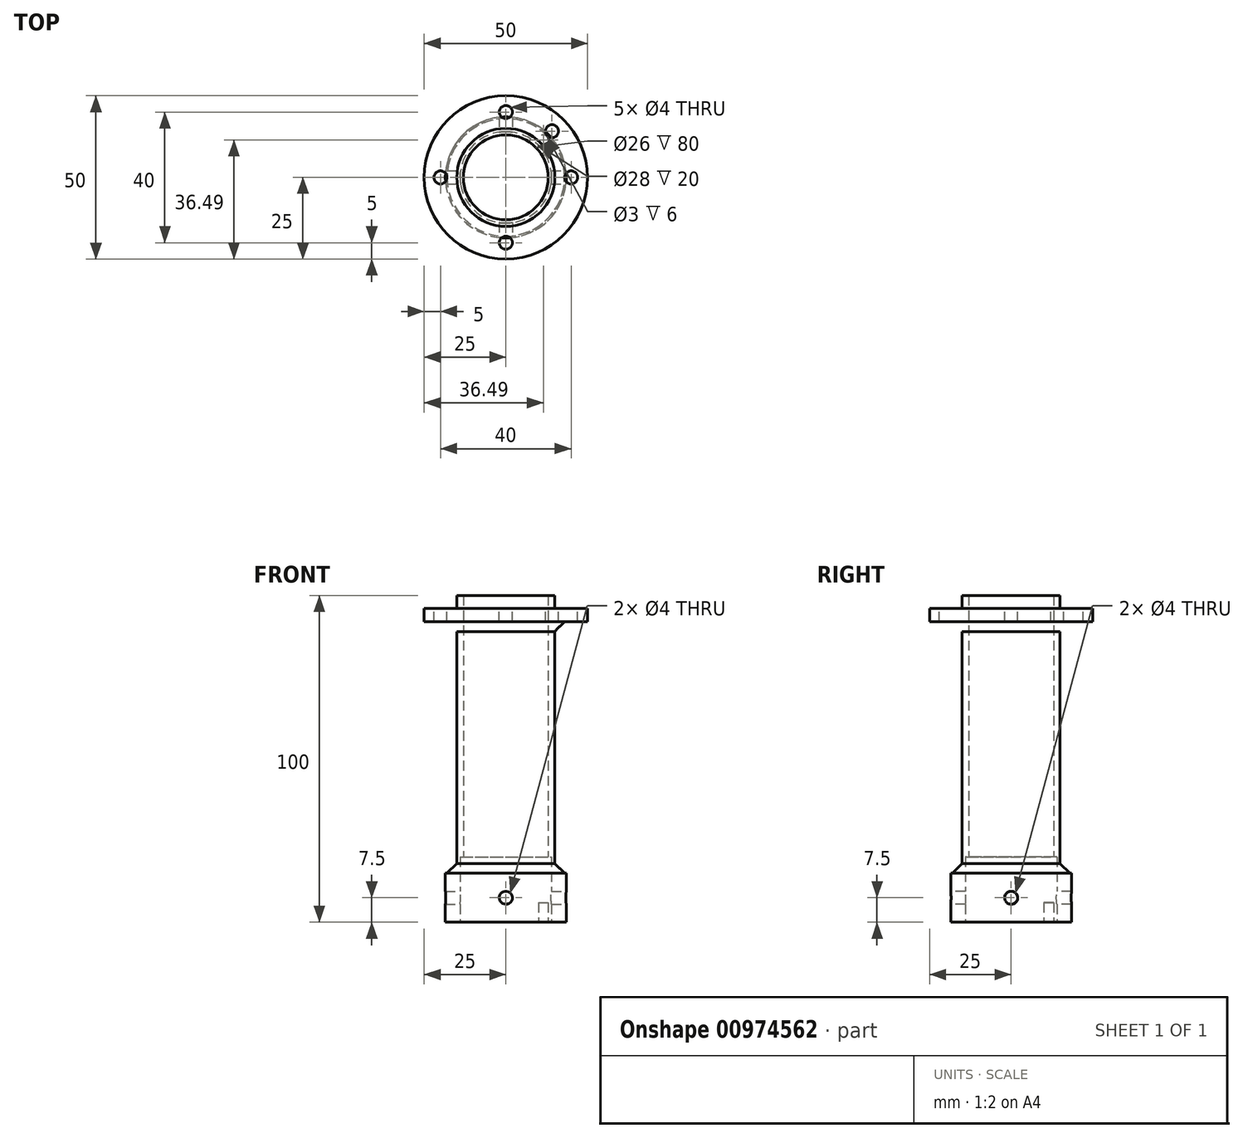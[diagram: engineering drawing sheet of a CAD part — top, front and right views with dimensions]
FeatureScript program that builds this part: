
annotation { "Feature Type Name" : "Feature", "Feature Type Description" : "" }
export const myFeature = defineFeature(function(context is Context, id is Id, definition is map)
    precondition{}
    {
        {
            var Q0;
            Q0=qCreatedBy(makeId("Top.planeOp"),FACE);
            var sketch = newSketch(context, id + "F0", { "sketchPlane" : qUnion([Q0])});
            skCircle(sketch, "E0", {"center": v(0, 0) * mm, "radius": 13 * mm});
            skCircle(sketch, "E1", {"center": v(0, 0) * mm, "radius": 15 * mm});
            skSolve(sketch);
        }
        {
            var Q0;
            Q0 = qSketchRegion(id + "F0", true);
            extrude(context, id + "F1", {"entities" : qUnion([Q0]), "depth" : 100 * mm, "offsetDistance" : 25 * mm});
        }
        {
            var Q0;
            Q0=makeQuery(id+"F1.opExtrude","CAP_FACE",FACE,{"disambiguationData":[OSD([sQuery(id+"F0.wireOp",EDGE,"E0"),sQuery(id+"F0.wireOp",EDGE,"E1")])],"isStart":false});
            cPlane(context, id + "F2", {"entities" : qUnion([Q0]), "cplaneType" : CPlaneType.OFFSET, "offset" : 4 * mm, "oppositeDirection" : true, "width" : 150 * mm, "height" : 150 * mm});
        }
        {
            var Q0;
            Q0=qCreatedBy(id+"F2.planeOp",FACE);
            var sketch = newSketch(context, id + "F3", { "sketchPlane" : qUnion([Q0])});
            skCircle(sketch, "E2", {"center": v(0, 0) * mm, "radius": 25 * mm});
            skCircle(sketch, "E3.0", {"center": v(0, 0) * mm, "radius": 15 * mm});
            skSolve(sketch);
        }
        {
            var Q0;
            Q0 = qSketchRegion(id + "F3", true);
            extrude(context, id + "F4", {"entities" : qUnion([Q0]), "operationType" : NewBodyOperationType.ADD, "oppositeDirection" : true, "depth" : 4 * mm, "offsetDistance" : 25 * mm});
        }
        {
            var Q0;
            Q0=makeQuery(id+"F4.opExtrude","CAP_FACE",FACE,{"disambiguationData":[OSD([sQuery(id+"F3.wireOp",EDGE,"E2"),sQuery(id+"F3.wireOp",EDGE,"E3.0")])],"isStart":true});
            var sketch = newSketch(context, id + "F5", { "sketchPlane" : qUnion([Q0])});
            skCircle(sketch, "E4", {"center": v(0, 20) * mm, "radius": 2 * mm});
            skCircle(sketch, "E5.1.0", {"center": v(-20, 0) * mm, "radius": 2 * mm});
            skCircle(sketch, "E5.2.0", {"center": v(0, -20) * mm, "radius": 2 * mm});
            skCircle(sketch, "E5.3.0", {"center": v(20, 0) * mm, "radius": 2 * mm});
            skPoint(sketch, "E5.center", {"position": v(0, 0) * mm});
            skSolve(sketch);
        }
        {
            var Q0;
            Q0 = qSketchRegion(id + "F5", true);
            extrude(context, id + "F6", {"entities" : qUnion([Q0]), "operationType" : NewBodyOperationType.REMOVE, "endBound" : BoundingType.THROUGH_ALL, "oppositeDirection" : true, "depth" : 25 * mm, "offsetDistance" : 25 * mm});
        }
        {
            var Q0;
            Q0=qCreatedBy(makeId("Top.planeOp"),FACE);
            var sketch = newSketch(context, id + "F7", { "sketchPlane" : qUnion([Q0])});
            skCircle(sketch, "E6", {"center": v(0, 0) * mm, "radius": 18.5 * mm});
            skCircle(sketch, "E7.0", {"center": v(0, 0) * mm, "radius": 13 * mm});
            skSolve(sketch);
        }
        {
            var Q0;
            Q0 = qSketchRegion(id + "F7", true);
            extrude(context, id + "F8", {"entities" : qUnion([Q0]), "operationType" : NewBodyOperationType.ADD, "depth" : 15 * mm, "offsetDistance" : 25 * mm});
        }
        {
            var Q0;
            Q0=qCreatedBy(makeId("Right.planeOp"),FACE);
            var sketch = newSketch(context, id + "F9", { "sketchPlane" : qUnion([Q0])});
            skLineSegment(sketch, "E8", {"start": v(-13, 0) * mm, "end": v(-13, 150) * mm, "construction": true});
            skLineSegment(sketch, "E9", {"start": v(13, 150) * mm, "end": v(13, 0) * mm, "construction": true});
            skLineSegment(sketch, "E10", {"start": v(-18.5, 0) * mm, "end": v(-18.5, 15) * mm, "construction": true});
            skLineSegment(sketch, "E11", {"start": v(18.5, 15) * mm, "end": v(18.5, 0) * mm, "construction": true});
            skLineSegment(sketch, "E12", {"start": v(15.75, 21.45) * mm, "end": v(15.75, -7.93) * mm, "construction": true});
            skLineSegment(sketch, "E13", {"start": v(24.83, 7.5) * mm, "end": v(-29.09, 7.5) * mm, "construction": true});
            skLineSegment(sketch, "E14", {"start": v(-15.75, 20.66) * mm, "end": v(-15.75, -8.82) * mm, "construction": true});
            skCircle(sketch, "E15", {"center": v(0, 7.5) * mm, "radius": 2 * mm});
            skSolve(sketch);
        }
        {
            var Q0;
            Q0 = qSketchRegion(id + "F9", true);
            extrude(context, id + "F10", {"entities" : qUnion([Q0]), "operationType" : NewBodyOperationType.REMOVE, "endBound" : BoundingType.SYMMETRIC, "oppositeDirection" : true, "depth" : 100 * mm, "offsetDistance" : 25 * mm});
        }
        {
            var Q0;
            Q0=qCreatedBy(makeId("Front.planeOp"),FACE);
            var sketch = newSketch(context, id + "F11", { "sketchPlane" : qUnion([Q0])});
            skLineSegment(sketch, "E16.0", {"start": v(-18.5, 15) * mm, "end": v(18.5, 15) * mm, "construction": true});
            skLineSegment(sketch, "E17.0", {"start": v(-18.5, 0) * mm, "end": v(18.5, 0) * mm, "construction": true});
            skLineSegment(sketch, "E18", {"start": v(-28.48, 7.5) * mm, "end": v(33.33, 7.5) * mm, "construction": true});
            skCircle(sketch, "E19", {"center": v(0, 7.5) * mm, "radius": 2 * mm});
            skSolve(sketch);
        }
        {
            var Q0;
            Q0 = qSketchRegion(id + "F11", true);
            extrude(context, id + "F12", {"entities" : qUnion([Q0]), "operationType" : NewBodyOperationType.REMOVE, "endBound" : BoundingType.SYMMETRIC, "oppositeDirection" : true, "depth" : 100 * mm, "offsetDistance" : 25 * mm});
        }
        {
            var Q0;
            Q0=makeQuery(id+"F4.opExtrude","CAP_EDGE",EDGE,{"disambiguationData":[OSD([sQuery(id+"F3.wireOp",EDGE,"E3.0")])],"isStart":false});
            chamfer(context, id + "F13", {"entities" : qUnion([Q0]), "width" : 3 * mm, "tangentPropagation" : true});
        }
        {
            var Q0;
            {var subQ0=sQuery(id+"F0.wireOp",EDGE,"E1");Q0=makeQuery(id+"F8.boolean.opBoolean","INTERSECT",EDGE,{"derivedFrom":[makeQuery(id+"F4.boolean.opBoolean","SPLIT",FACE,{"disambiguationData":[TD([makeQuery(id+"F1.opExtrude","CAP_FACE",FACE,{"disambiguationData":[OSD([sQuery(id+"F0.wireOp",EDGE,"E0"),subQ0])],"isStart":true})])],"derivedFrom":makeQuery(id+"F1.opExtrude","SWEPT_FACE",FACE,{"disambiguationData":[OSD([subQ0])]})}),makeQuery(id+"F8.opExtrude","CAP_FACE",FACE,{"disambiguationData":[OSD([sQuery(id+"F7.wireOp",EDGE,"E6"),sQuery(id+"F7.wireOp",EDGE,"E7.0")])],"isStart":false})]});}
            chamfer(context, id + "F14", {"entities" : qUnion([Q0]), "width" : 3 * mm, "tangentPropagation" : true});
        }
        {
            var Q0;
            Q0=makeQuery(id+"F8.boolean.opBoolean","MERGE",FACE,{"derivedFrom":[makeQuery(id+"F1.opExtrude","CAP_FACE",FACE,{"disambiguationData":[OSD([sQuery(id+"F0.wireOp",EDGE,"E0"),sQuery(id+"F0.wireOp",EDGE,"E1")])],"isStart":true}),makeQuery(id+"F8.opExtrude","CAP_FACE",FACE,{"disambiguationData":[OSD([sQuery(id+"F7.wireOp",EDGE,"E6"),sQuery(id+"F7.wireOp",EDGE,"E7.0")])],"isStart":true})]});
            var sketch = newSketch(context, id + "F15", { "sketchPlane" : qUnion([Q0])});
            skCircle(sketch, "E20", {"center": v(0, 0) * mm, "radius": 14 * mm});
            skSolve(sketch);
        }
        {
            var Q0;
            Q0 = qSketchRegion(id + "F15", true);
            extrude(context, id + "F16", {"entities" : qUnion([Q0]), "operationType" : NewBodyOperationType.REMOVE, "oppositeDirection" : true, "depth" : 20 * mm, "offsetDistance" : 25 * mm});
        }
        {
            var Q0;
            Q0=makeQuery(id+"F4.opExtrude","CAP_FACE",FACE,{"disambiguationData":[OSD([sQuery(id+"F3.wireOp",EDGE,"E2"),sQuery(id+"F3.wireOp",EDGE,"E3.0")])],"isStart":true});
            var sketch = newSketch(context, id + "F17", { "sketchPlane" : qUnion([Q0])});
            skCircle(sketch, "E21", {"center": v(0, 0) * mm, "radius": 20 * mm, "construction": true});
            skLineSegment(sketch, "E22", {"start": v(0, 0) * mm, "end": v(31.82, 31.82) * mm, "construction": true});
            skCircle(sketch, "E23", {"center": v(14.14, 14.14) * mm, "radius": 2 * mm});
            skSolve(sketch);
        }
        {
            var Q0;
            Q0 = qSketchRegion(id + "F17", true);
            extrude(context, id + "F18", {"entities" : qUnion([Q0]), "operationType" : NewBodyOperationType.REMOVE, "oppositeDirection" : true, "depth" : 25 * mm, "offsetDistance" : 25 * mm});
        }
        {
            var Q0;
            Q0=makeQuery(id+"F8.boolean.opBoolean","MERGE",FACE,{"derivedFrom":[makeQuery(id+"F1.opExtrude","CAP_FACE",FACE,{"disambiguationData":[OSD([sQuery(id+"F0.wireOp",EDGE,"E0"),sQuery(id+"F0.wireOp",EDGE,"E1")])],"isStart":true}),makeQuery(id+"F8.opExtrude","CAP_FACE",FACE,{"disambiguationData":[OSD([sQuery(id+"F7.wireOp",EDGE,"E6"),sQuery(id+"F7.wireOp",EDGE,"E7.0")])],"isStart":true})]});
            var sketch = newSketch(context, id + "F19", { "sketchPlane" : qUnion([Q0])});
            skCircle(sketch, "E24", {"center": v(0, 0) * mm, "radius": 16.25 * mm, "construction": true});
            skLineSegment(sketch, "E25", {"start": v(0, 0) * mm, "end": v(27.25, -27.25) * mm, "construction": true});
            skCircle(sketch, "E26", {"center": v(11.5, -11.5) * mm, "radius": 1.5 * mm});
            skSolve(sketch);
        }
        {
            var Q0;
            Q0 = qSketchRegion(id + "F19", true);
            extrude(context, id + "F20", {"entities" : qUnion([Q0]), "operationType" : NewBodyOperationType.REMOVE, "oppositeDirection" : true, "depth" : 6 * mm, "offsetDistance" : 25 * mm});
        }
    });
